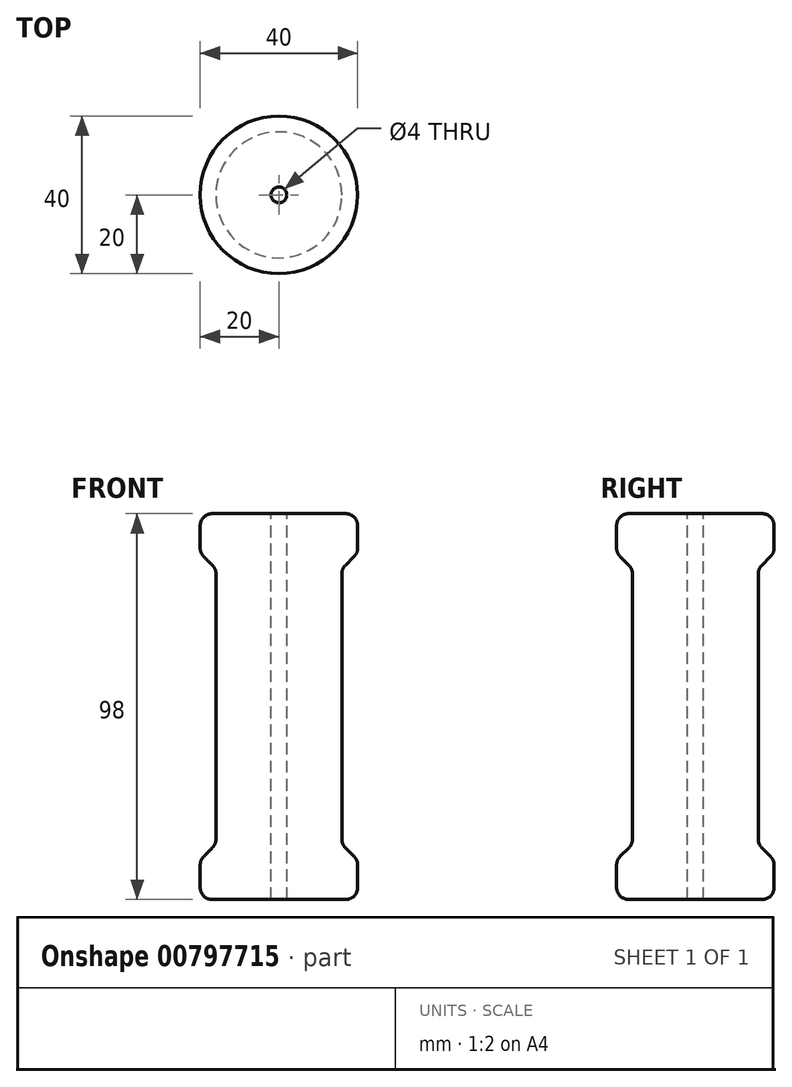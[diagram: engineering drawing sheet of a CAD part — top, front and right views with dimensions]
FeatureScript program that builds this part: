
annotation { "Feature Type Name" : "Feature", "Feature Type Description" : "" }
export const myFeature = defineFeature(function(context is Context, id is Id, definition is map)
    precondition{}
    {
        {
            var Q0;
            Q0=qCreatedBy(makeId("Front.planeOp"),FACE);
            var sketch = newSketch(context, id + "F0", { "sketchPlane" : qUnion([Q0])});
            skLineSegment(sketch, "E0", {"start": v(0, 37.01) * mm, "end": v(0, -37.13) * mm, "construction": true});
            skLineSegment(sketch, "E1", {"start": v(-16, 35) * mm, "end": v(-16, 0) * mm});
            skLineSegment(sketch, "E2", {"start": v(-21.75, 0) * mm, "end": v(20.94, 0) * mm, "construction": true});
            skLineSegment(sketch, "E3", {"start": v(-16, 35) * mm, "end": v(-20, 39) * mm});
            skLineSegment(sketch, "E4", {"start": v(-20, 39) * mm, "end": v(-20, 49) * mm});
            skLineSegment(sketch, "E5", {"start": v(-20, 49) * mm, "end": v(-2, 49) * mm});
            skLineSegment(sketch, "E6", {"start": v(-2, 49) * mm, "end": v(-2, 0) * mm});
            skLineSegment(sketch, "E7.MirrorCS", {"start": v(-16, -35) * mm, "end": v(-16, 0) * mm});
            skLineSegment(sketch, "E8.MirrorCS", {"start": v(-16, -35) * mm, "end": v(-20, -39) * mm});
            skLineSegment(sketch, "E9.MirrorCS", {"start": v(-20, -39) * mm, "end": v(-20, -49) * mm});
            skLineSegment(sketch, "E10.MirrorCS", {"start": v(-20, -49) * mm, "end": v(-2, -49) * mm});
            skLineSegment(sketch, "E11.MirrorCS", {"start": v(-2, -49) * mm, "end": v(-2, 0) * mm});
            skSolve(sketch);
        }
        {
            var Q0;
            Q0=makeQuery(id+"F0.imprint","IMPRINT",FACE,{"disambiguationData":[TD([[makeQuery(id+"F0.imprint","IMPRINT",EDGE,{"derivedFrom":sQuery(id+"F0.wireOp",EDGE,"E1")}),1.0]])]});
            var Q1;
            Q1=sQuery(id+"F0.wireOp",EDGE,"E0");
            revolve(context, id + "F1", {"surfaceOperationType" : NewSurfaceOperationType.NEW, "entities" : qUnion([Q0]), "axis" : qUnion([Q1]), "revolveType" : RevolveType.FULL});
        }
        {
            var Q0;
            Q0=makeQuery(id+"F1.opRevolve","SWEPT_EDGE",EDGE,{"disambiguationData":[OSD([sQuery(id+"F0.wireOp",EDGE,"E1"),sQuery(id+"F0.wireOp",EDGE,"E3")])]});
            var Q1;
            Q1=makeQuery(id+"F1.opRevolve","SWEPT_EDGE",EDGE,{"disambiguationData":[OSD([sQuery(id+"F0.wireOp",EDGE,"E7.MirrorCS"),sQuery(id+"F0.wireOp",EDGE,"E8.MirrorCS")])]});
            var Q2;
            Q2=makeQuery(id+"F1.opRevolve","SWEPT_EDGE",EDGE,{"disambiguationData":[OSD([sQuery(id+"F0.wireOp",EDGE,"E8.MirrorCS"),sQuery(id+"F0.wireOp",EDGE,"E9.MirrorCS")])]});
            var Q3;
            Q3=makeQuery(id+"F1.opRevolve","SWEPT_EDGE",EDGE,{"disambiguationData":[OSD([sQuery(id+"F0.wireOp",EDGE,"E9.MirrorCS"),sQuery(id+"F0.wireOp",EDGE,"E10.MirrorCS")])]});
            var Q4;
            Q4=makeQuery(id+"F1.opRevolve","SWEPT_EDGE",EDGE,{"disambiguationData":[OSD([sQuery(id+"F0.wireOp",EDGE,"E3"),sQuery(id+"F0.wireOp",EDGE,"E4")])]});
            var Q5;
            Q5=makeQuery(id+"F1.opRevolve","SWEPT_EDGE",EDGE,{"disambiguationData":[OSD([sQuery(id+"F0.wireOp",EDGE,"E4"),sQuery(id+"F0.wireOp",EDGE,"E5")])]});
            fillet(context, id + "F2", {"entities" : qUnion([Q0, Q1, Q2, Q3, Q4, Q5]), "radius" : 3 * mm, "tangentPropagation" : true, "allowEdgeOverflow" : false});
        }
    });
